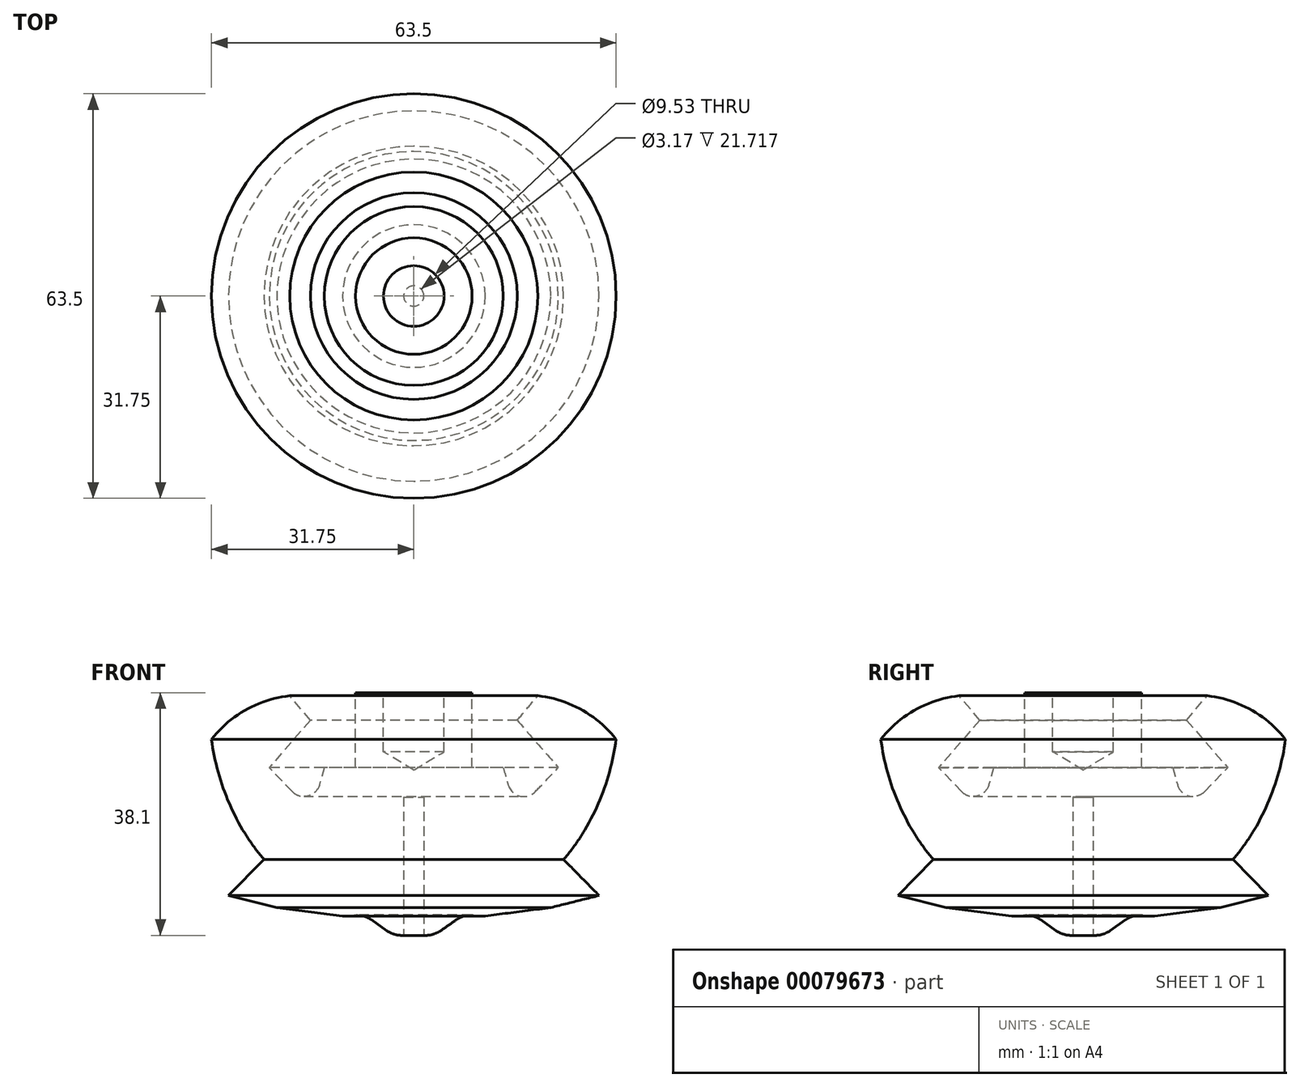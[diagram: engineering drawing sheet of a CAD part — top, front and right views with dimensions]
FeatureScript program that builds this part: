
annotation { "Feature Type Name" : "Feature", "Feature Type Description" : "" }
export const myFeature = defineFeature(function(context is Context, id is Id, definition is map)
    precondition{}
    {
        {
            var Q0;
            Q0=qCreatedBy(makeId("Front.planeOp"),FACE);
            var sketch = newSketch(context, id + "F0", { "sketchPlane" : qUnion([Q0])});
            skLineSegment(sketch, "E0", {"start": v(0, 0) * mm, "end": v(0, -26.35) * mm});
            skPoint(sketch, "E1.orphan", {"position": v(0, 28.58) * mm});
            skLineSegment(sketch, "E2", {"start": v(-3.17, -26.35) * mm, "end": v(-7.88, -23.06) * mm});
            skPoint(sketch, "E3.end.orphan", {"position": v(0, 15.93) * mm});
            skLineSegment(sketch, "E4", {"start": v(-9.15, 11.75) * mm, "end": v(0, 11.75) * mm});
            skLineSegment(sketch, "E5", {"start": v(0, 11.75) * mm, "end": v(0, 0) * mm});
            skLineSegment(sketch, "E6", {"start": v(-3.17, -26.35) * mm, "end": v(0, -26.35) * mm});
            skPoint(sketch, "E7.end.orphan", {"position": v(-22.68, 11.75) * mm});
            skLineSegment(sketch, "E8", {"start": v(-22.68, 0) * mm, "end": v(-16.02, -6.99) * mm});
            skLineSegment(sketch, "E9", {"start": v(-14.04, 0) * mm, "end": v(-16.02, -6.99) * mm});
            skLineSegment(sketch, "E10", {"start": v(-9.15, 11.75) * mm, "end": v(-9.15, 0) * mm});
            skLineSegment(sketch, "E11", {"start": v(-9.15, 0) * mm, "end": v(-14.04, 0) * mm});
            skLineSegment(sketch, "E12", {"start": v(-19.46, 11.25) * mm, "end": v(-16.23, 7.4) * mm});
            skLineSegment(sketch, "E13", {"start": v(-16.23, 7.4) * mm, "end": v(-22.68, 0) * mm});
            skArc(sketch, "E14", {"start": v(-19.46, 11.25) * mm, "mid": v(-26.3, 9.08) * mm, "end": v(-31.75, 4.42) * mm});
            skPoint(sketch, "E15.start.orphan", {"position": v(-22.68, 7.3) * mm});
            skArc(sketch, "E16", {"start": v(-31.75, 4.42) * mm, "mid": v(-30.02, -2.92) * mm, "end": v(-26.85, -9.77) * mm});
            skLineSegment(sketch, "E17", {"start": v(-11.2, -23.32) * mm, "end": v(-7.88, -23.06) * mm});
            skArc(sketch, "E18", {"start": v(-26.85, -9.77) * mm, "mid": v(-25.28, -12.18) * mm, "end": v(-23.5, -14.44) * mm});
            skLineSegment(sketch, "E19", {"start": v(-21.5, -21.99) * mm, "end": v(-11.2, -23.32) * mm});
            skLineSegment(sketch, "E20", {"start": v(-23.5, -14.44) * mm, "end": v(-29.08, -20.1) * mm});
            skLineSegment(sketch, "E21", {"start": v(-29.08, -20.1) * mm, "end": v(-21.5, -21.99) * mm});
            skPoint(sketch, "E22.end.orphan", {"position": v(-21.5, -21.07) * mm});
            skSolve(sketch);
        }
        {
            var Q0;
            Q0=makeQuery(id+"F0.imprint","IMPRINT",FACE,{"disambiguationData":[TD([[makeQuery(id+"F0.imprint","IMPRINT",EDGE,{"derivedFrom":sQuery(id+"F0.wireOp",EDGE,"E0")}),-1.0]])]});
            var Q1;
            Q1=sQuery(id+"F0.wireOp",EDGE,"E5");
            revolve(context, id + "F1", {"entities" : qUnion([Q0]), "axis" : qUnion([Q1]), "revolveType" : RevolveType.FULL});
        }
        {
            var Q0;
            Q0=makeQuery(id+"F1.opRevolve","SWEPT_FACE",FACE,{"disambiguationData":[OSD([sQuery(id+"F0.wireOp",EDGE,"E4")])]});
            var sketch = newSketch(context, id + "F2", { "sketchPlane" : qUnion([Q0])});
            skCircle(sketch, "E23", {"center": v(0, 0) * mm, "radius": 1.59 * mm});
            skSolve(sketch);
        }
        {
            var Q0;
            Q0=sQuery(id+"F2.wireOp",VERTEX,"E23.center");
            var Q1;
            Q1=makeQuery(id+"F1.opRevolve","SWEPT_BODY",BODY,{"disambiguationData":[OSD([sQuery(id+"F0.wireOp",EDGE,"HhWg7zB1-15oS-yYAK-8FMO-IT7WBvzD5zCt"),sQuery(id+"F0.wireOp",EDGE,"E0"),sQuery(id+"F0.wireOp",EDGE,"E2"),sQuery(id+"F0.wireOp",EDGE,"ThBTcP4O-k3SS-3l5J-zT9Y-G8tZuwIAeMhn"),sQuery(id+"F0.wireOp",EDGE,"E4"),sQuery(id+"F0.wireOp",EDGE,"E5"),sQuery(id+"F0.wireOp",EDGE,"E6")])]});
            hole(context, id + "F3", {"style" : HoleStyle.SIMPLE, "endStyle" : HoleEndStyle.BLIND, "holeDiameter" : 9.52 * mm, "holeDepth" : 9.27 * mm, "locations" : qUnion([Q0]), "scope" : qUnion([Q1])});
        }
        {
            var Q0;
            Q0=makeQuery(id+"F1.opRevolve","SWEPT_FACE",FACE,{"disambiguationData":[OSD([sQuery(id+"F0.wireOp",EDGE,"E6")])]});
            var sketch = newSketch(context, id + "F4", { "sketchPlane" : qUnion([Q0])});
            skCircle(sketch, "E24", {"center": v(0, 0) * mm, "radius": 1.59 * mm});
            skSolve(sketch);
        }
        {
            var Q0;
            Q0=makeQuery(id+"F4.imprint","IMPRINT",FACE,{"disambiguationData":[TD([[makeQuery(id+"F4.imprint","IMPRINT",EDGE,{"derivedFrom":sQuery(id+"F4.wireOp",EDGE,"E24")}),1.0]])]});
            extrude(context, id + "F5", {"entities" : qUnion([Q0]), "operationType" : NewBodyOperationType.REMOVE, "oppositeDirection" : true, "depth" : 21.72 * mm});
        }
        {
            var Q0;
            Q0=makeQuery(id+"F1.opRevolve","SWEPT_EDGE",EDGE,{"disambiguationData":[OSD([sQuery(id+"F0.wireOp",EDGE,"E8"),sQuery(id+"F0.wireOp",EDGE,"E9")])]});
            fillet(context, id + "F6", {"entities" : qUnion([Q0]), "radius" : 2.54 * mm, "tangentPropagation" : true, "allowEdgeOverflow" : false});
        }
        {
            var Q0;
            Q0=makeQuery(id+"F1.opRevolve","SWEPT_EDGE",EDGE,{"disambiguationData":[OSD([sQuery(id+"F0.wireOp",EDGE,"E2"),sQuery(id+"F0.wireOp",EDGE,"w2wifkOz-v00W-wPYe-Hra8-Z6pEqpDBSaJI")])]});
            fillet(context, id + "F7", {"entities" : qUnion([Q0]), "radius" : 4.2 * mm, "tangentPropagation" : true, "allowEdgeOverflow" : false});
        }
    });
